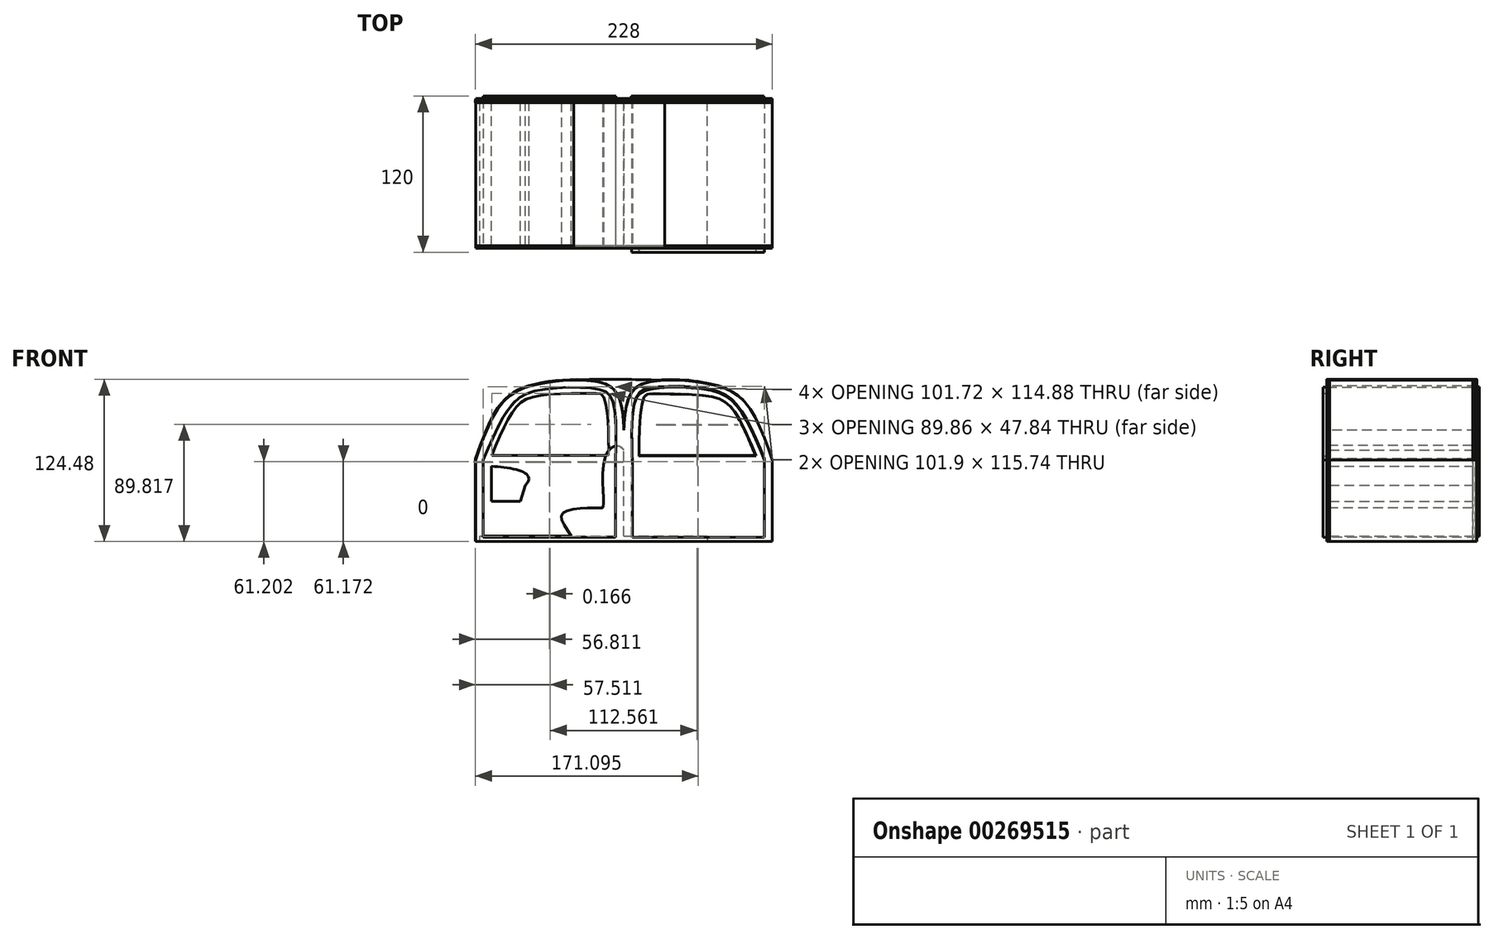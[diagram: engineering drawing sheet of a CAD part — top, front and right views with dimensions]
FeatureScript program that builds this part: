
annotation { "Feature Type Name" : "Feature", "Feature Type Description" : "" }
export const myFeature = defineFeature(function(context is Context, id is Id, definition is map)
    precondition{}
    {
        {
            var Q0;
            Q0=qCreatedBy(makeId("Front.planeOp"),FACE);
            var sketch = newSketch(context, id + "F0", { "sketchPlane" : qUnion([Q0])});
            skLineSegment(sketch, "E0.bottom", {"start": v(-52.37, -30.32) * mm, "end": v(58, -30.32) * mm});
            skLineSegment(sketch, "E0.top", {"start": v(-52.37, 75.93) * mm, "end": v(58, 75.93) * mm});
            skLineSegment(sketch, "E0.left", {"start": v(-52.37, -30.32) * mm, "end": v(-52.37, 75.93) * mm});
            skLineSegment(sketch, "E0.right", {"start": v(58, -30.32) * mm, "end": v(58, 75.93) * mm});
            skLineSegment(sketch, "E1", {"start": v(-52.37, -26.56) * mm, "end": v(17.83, -26.56) * mm});
            skFitSpline(sketch, "E2", {"points": [v(17.83, -26.56) * mm, v(11.64, -8.73) * mm, v(39.8, -5.16) * mm, v(42.43, -3.66) * mm, v(45.05, 37.08) * mm, v(58, 39.52) * mm, v(58, 9.86) * mm], "startDerivative": vector(-102.72, 146.21) * mm, "endDerivative": vector(-61.38, 44.33) * mm});
            skLineSegment(sketch, "E3", {"start": v(58, -26.56) * mm, "end": v(122.26, -26.56) * mm});
            skLineSegment(sketch, "E4", {"start": v(122.26, -26.56) * mm, "end": v(122.26, -30.32) * mm});
            skLineSegment(sketch, "E5", {"start": v(122.26, -30.32) * mm, "end": v(58, -30.32) * mm});
            skSolve(sketch);
        }
        {
            var Q0;
            {var subQ2=sQuery(id+"F0.wireOp",EDGE,"E0.bottom");Q0=makeQuery(id+"F0.imprint","IMPRINT",FACE,{"disambiguationData":[TD([[makeQuery(id+"F0.imprint","IMPRINT",EDGE,{"derivedFrom":subQ2}),1.0]])]});}
            var Q1;
            {var subQ2=sQuery(id+"F0.wireOp",EDGE,"E3");Q1=makeQuery(id+"F0.imprint","IMPRINT",FACE,{"disambiguationData":[TD([[makeQuery(id+"F0.imprint","IMPRINT",EDGE,{"derivedFrom":subQ2}),-1.0]])]});}
            var Q2;
            Q2=qSketchRegion(id+"F2",true);
            extrude(context, id + "F1", {"entities" : qUnion([Q0, Q1, Q2]), "endBound" : BoundingType.SYMMETRIC, "depth" : 110 * mm});
        }
        {
            var Q0;
            Q0=makeQuery(id+"F1.opExtrude","CAP_FACE",FACE,{"disambiguationData":[OSD([sQuery(id+"F0.wireOp",EDGE,"E0.bottom"),sQuery(id+"F0.wireOp",EDGE,"E0.left"),sQuery(id+"F0.wireOp",EDGE,"E0.right"),sQuery(id+"F0.wireOp",EDGE,"E1"),sQuery(id+"F0.wireOp",EDGE,"E2")])],"isStart":true});
            var sketch = newSketch(context, id + "F2", { "sketchPlane" : qUnion([Q0])});
            skLineSegment(sketch, "E6", {"start": v(21.37, 0) * mm, "end": v(17.65, 12.48) * mm});
            skFitSpline(sketch, "E7", {"points": [v(17.65, 12.48) * mm, v(14.83, 16.43) * mm, v(17.65, 21.68) * mm, v(43.55, 26.94) * mm, v(64.2, 27.5) * mm], "startDerivative": vector(-24.47, 23.82) * mm, "endDerivative": vector(59, 0.05) * mm});
            skPoint(sketch, "E8.right.end.orphan", {"position": v(30.41, 0) * mm});
            skLineSegment(sketch, "E9", {"start": v(21.37, 0) * mm, "end": v(43.55, 0) * mm});
            skLineSegment(sketch, "E10", {"start": v(43.55, 26.94) * mm, "end": v(43.55, 0) * mm});
            skSolve(sketch);
        }
        {
            var Q0;
            Q0=qSketchRegion(id+"F2",true);
            extrude(context, id + "F3", {"entities" : qUnion([Q0]), "oppositeDirection" : true, "depth" : 110 * mm});
        }
        {
            var Q0;
            Q0=makeQuery(id+"F1.opExtrude","CAP_FACE",FACE,{"disambiguationData":[OSD([sQuery(id+"F0.wireOp",EDGE,"E0.bottom"),sQuery(id+"F0.wireOp",EDGE,"E0.left"),sQuery(id+"F0.wireOp",EDGE,"E0.right"),sQuery(id+"F0.wireOp",EDGE,"E1"),sQuery(id+"F0.wireOp",EDGE,"E2"),sQuery(id+"F0.wireOp",EDGE,"E3"),sQuery(id+"F0.wireOp",EDGE,"E4"),sQuery(id+"F0.wireOp",EDGE,"E5")])],"isStart":false});
            var sketch = newSketch(context, id + "F4", { "sketchPlane" : qUnion([Q0])});
            skLineSegment(sketch, "E11.bottom", {"start": v(51.77, -27.48) * mm, "end": v(-49.8, -27.48) * mm});
            skLineSegment(sketch, "E11.left", {"start": v(51.77, -27.48) * mm, "end": v(51.77, 31.84) * mm});
            skLineSegment(sketch, "E11.right", {"start": v(-49.8, -27.48) * mm, "end": v(-49.8, 31.84) * mm});
            skFitSpline(sketch, "E12", {"points": [v(-49.8, 31.84) * mm, v(-29.14, 72.58) * mm, v(-8.12, 85.15) * mm, v(37.12, 86.28) * mm, v(48.95, 78.58) * mm, v(51.77, 31.84) * mm], "startDerivative": vector(85.44, 201.79) * mm, "endDerivative": vector(-6.45, -241.46) * mm});
            skLineSegment(sketch, "E13.top", {"start": v(-55.74, -30.78) * mm, "end": v(58.17, -30.78) * mm});
            skLineSegment(sketch, "E13.left", {"start": v(-55.74, 31.84) * mm, "end": v(-55.74, -30.78) * mm});
            skLineSegment(sketch, "E13.right", {"start": v(58.17, 31.84) * mm, "end": v(58.17, -30.78) * mm});
            skFitSpline(sketch, "E14", {"points": [v(-55.74, 31.84) * mm, v(-35.95, 74.78) * mm, v(-9.12, 89.73) * mm, v(37.12, 91.93) * mm, v(53.77, 80.94) * mm, v(58.17, 31.84) * mm], "startDerivative": vector(76.78, 219.74) * mm, "endDerivative": vector(-3.68, -254.2) * mm});
            skFitSpline(sketch, "E15.MirrorCS", {"points": [v(172.09, 31.84) * mm, v(152.3, 74.78) * mm, v(125.47, 89.73) * mm, v(79.22, 91.93) * mm, v(62.57, 80.94) * mm, v(58.17, 31.84) * mm], "startDerivative": vector(-76.78, 219.74) * mm, "endDerivative": vector(3.68, -254.2) * mm});
            skFitSpline(sketch, "E16.MirrorCS", {"points": [v(166.14, 31.84) * mm, v(145.49, 72.58) * mm, v(124.46, 85.15) * mm, v(79.22, 86.28) * mm, v(67.4, 78.58) * mm, v(64.58, 31.84) * mm], "startDerivative": vector(-85.44, 201.79) * mm, "endDerivative": vector(6.45, -241.46) * mm});
            skLineSegment(sketch, "E17.MirrorCS", {"start": v(64.58, -27.48) * mm, "end": v(64.58, 31.84) * mm});
            skLineSegment(sketch, "E18.MirrorCS", {"start": v(64.58, -27.48) * mm, "end": v(166.14, -27.48) * mm});
            skLineSegment(sketch, "E19.MirrorCS", {"start": v(172.09, -30.78) * mm, "end": v(58.17, -30.78) * mm});
            skLineSegment(sketch, "E20.MirrorCS", {"start": v(172.09, 31.84) * mm, "end": v(172.09, -30.78) * mm});
            skLineSegment(sketch, "E21.MirrorCS", {"start": v(166.14, -27.48) * mm, "end": v(166.14, 31.84) * mm});
            skLineSegment(sketch, "E22.right", {"start": v(58.42, 31.84) * mm, "end": v(58.42, -30.78) * mm});
            skFitSpline(sketch, "E23", {"points": [v(-49.8, 31.84) * mm, v(-29.14, 72.58) * mm, v(-8.12, 85.15) * mm, v(37.12, 86.28) * mm, v(48.95, 78.58) * mm, v(51.77, 31.84) * mm], "startDerivative": vector(85.44, 201.79) * mm, "endDerivative": vector(-6.45, -241.46) * mm});
            skFitSpline(sketch, "E24", {"points": [v(-43.16, 34.84) * mm, v(-25.58, 70.51) * mm, v(-8.12, 80.46) * mm, v(34.68, 82.53) * mm, v(43.5, 78.2) * mm, v(46.7, 34.66) * mm, v(46.7, 34.47) * mm], "startDerivative": vector(74.67, 181.05) * mm, "endDerivative": vector(0.05, -3.93) * mm});
            skLineSegment(sketch, "E25", {"start": v(-43.16, 34.84) * mm, "end": v(46.7, 34.66) * mm});
            skLineSegment(sketch, "E26.left", {"start": v(64.58, -26.56) * mm, "end": v(64.58, 32.76) * mm});
            skFitSpline(sketch, "E27.MirrorCS", {"points": [v(159.5, 35.76) * mm, v(141.92, 71.43) * mm, v(124.46, 81.38) * mm, v(81.66, 83.44) * mm, v(72.84, 79.13) * mm, v(69.65, 35.57) * mm, v(69.65, 35.39) * mm], "startDerivative": vector(-74.67, 181.05) * mm, "endDerivative": vector(-0.05, -3.93) * mm});
            skLineSegment(sketch, "E28.MirrorCS", {"start": v(159.5, 35.76) * mm, "end": v(69.65, 35.57) * mm});
            skFitSpline(sketch, "E29.MirrorCS", {"points": [v(166.14, 32.76) * mm, v(145.49, 73.5) * mm, v(124.46, 86.07) * mm, v(79.22, 87.2) * mm, v(67.4, 79.5) * mm, v(64.58, 32.76) * mm], "startDerivative": vector(-85.44, 201.79) * mm, "endDerivative": vector(6.45, -241.46) * mm});
            skLineSegment(sketch, "E30.MirrorCS", {"start": v(166.14, -26.56) * mm, "end": v(166.14, 32.76) * mm});
            skLineSegment(sketch, "E31.MirrorCS", {"start": v(64.58, -26.56) * mm, "end": v(166.14, -26.56) * mm});
            skSolve(sketch);
        }
        {
            var Q0;
            Q0=qSketchRegion(id+"F4",true);
            extrude(context, id + "F5", {"entities" : qUnion([Q0]), "depth" : 2 * mm});
        }
        {
            var Q0;
            Q0=makeQuery(id+"F1.opExtrude","CAP_FACE",FACE,{"disambiguationData":[OSD([sQuery(id+"F0.wireOp",EDGE,"E0.bottom"),sQuery(id+"F0.wireOp",EDGE,"E0.left"),sQuery(id+"F0.wireOp",EDGE,"E0.right"),sQuery(id+"F0.wireOp",EDGE,"E1"),sQuery(id+"F0.wireOp",EDGE,"E2"),sQuery(id+"F0.wireOp",EDGE,"E3"),sQuery(id+"F0.wireOp",EDGE,"E4"),sQuery(id+"F0.wireOp",EDGE,"E5")])],"isStart":true});
            var sketch = newSketch(context, id + "F6", { "sketchPlane" : qUnion([Q0])});
            skLineSegment(sketch, "E32.right", {"start": v(-58, 32.3) * mm, "end": v(-58, -30.32) * mm});
            skFitSpline(sketch, "E33.MirrorCS", {"points": [v(55.9, 32.3) * mm, v(36.12, 75.24) * mm, v(9.29, 90.2) * mm, v(-36.96, 92.4) * mm, v(-53.6, 81.4) * mm, v(-58, 32.3) * mm], "startDerivative": vector(-76.78, 219.74) * mm, "endDerivative": vector(3.68, -254.2) * mm});
            skFitSpline(sketch, "E34.MirrorCS", {"points": [v(49.96, 32.3) * mm, v(29.3, 73.04) * mm, v(8.28, 85.62) * mm, v(-36.96, 86.74) * mm, v(-48.78, 79.05) * mm, v(-51.6, 32.3) * mm], "startDerivative": vector(-85.44, 201.79) * mm, "endDerivative": vector(6.45, -241.46) * mm});
            skLineSegment(sketch, "E35.MirrorCS", {"start": v(-51.6, -27.02) * mm, "end": v(-51.6, 32.3) * mm});
            skLineSegment(sketch, "E36.MirrorCS", {"start": v(-51.6, -27.02) * mm, "end": v(49.96, -27.02) * mm});
            skLineSegment(sketch, "E37.MirrorCS", {"start": v(55.9, -30.32) * mm, "end": v(-58, -30.32) * mm});
            skLineSegment(sketch, "E38.MirrorCS", {"start": v(55.9, 32.3) * mm, "end": v(55.9, -30.32) * mm});
            skLineSegment(sketch, "E39.MirrorCS", {"start": v(49.96, -27.02) * mm, "end": v(49.96, 32.3) * mm});
            skLineSegment(sketch, "E40.MirrorCS", {"start": v(-58.32, 32.3) * mm, "end": v(-58.32, -30.32) * mm});
            skLineSegment(sketch, "E41.bottom", {"start": v(-64.16, -27.02) * mm, "end": v(-165.72, -27.02) * mm});
            skLineSegment(sketch, "E41.left", {"start": v(-64.16, -27.02) * mm, "end": v(-64.16, 32.3) * mm});
            skLineSegment(sketch, "E41.right", {"start": v(-165.72, -27.02) * mm, "end": v(-165.72, 32.3) * mm});
            skFitSpline(sketch, "E42", {"points": [v(-165.72, 32.3) * mm, v(-145.07, 73.04) * mm, v(-124.05, 85.62) * mm, v(-78.8, 86.74) * mm, v(-66.98, 79.05) * mm, v(-64.16, 32.3) * mm], "startDerivative": vector(85.44, 201.79) * mm, "endDerivative": vector(-6.45, -241.46) * mm});
            skLineSegment(sketch, "E43.left", {"start": v(-171.67, 32.3) * mm, "end": v(-171.67, -30.32) * mm});
            skLineSegment(sketch, "E43.right", {"start": v(-57.76, 32.3) * mm, "end": v(-57.76, -30.32) * mm});
            skFitSpline(sketch, "E44", {"points": [v(-171.67, 32.3) * mm, v(-151.88, 75.24) * mm, v(-125.05, 90.2) * mm, v(-78.8, 92.4) * mm, v(-62.16, 81.4) * mm, v(-57.76, 32.3) * mm], "startDerivative": vector(76.78, 219.74) * mm, "endDerivative": vector(-3.68, -254.2) * mm});
            skLineSegment(sketch, "E45.MirrorCS", {"start": v(-171.67, -30.32) * mm, "end": v(-57.76, -30.32) * mm});
            skSolve(sketch);
        }
        {
            var Q0;
            Q0=qSketchRegion(id+"F6",true);
            extrude(context, id + "F7", {"entities" : qUnion([Q0]), "depth" : 2 * mm});
        }
        {
            var Q0;
            Q0=makeQuery(id+"F7.opExtrude","CAP_FACE",FACE,{"disambiguationData":[OSD([sQuery(id+"F6.wireOp",EDGE,"E33.MirrorCS"),sQuery(id+"F6.wireOp",EDGE,"E34.MirrorCS"),sQuery(id+"F6.wireOp",EDGE,"E35.MirrorCS"),sQuery(id+"F6.wireOp",EDGE,"E36.MirrorCS"),sQuery(id+"F6.wireOp",EDGE,"E37.MirrorCS"),sQuery(id+"F6.wireOp",EDGE,"E38.MirrorCS"),sQuery(id+"F6.wireOp",EDGE,"E39.MirrorCS"),sQuery(id+"F6.wireOp",EDGE,"E41.bottom"),sQuery(id+"F6.wireOp",EDGE,"E41.left"),sQuery(id+"F6.wireOp",EDGE,"E41.right"),sQuery(id+"F6.wireOp",EDGE,"E42"),sQuery(id+"F6.wireOp",EDGE,"E43.left"),sQuery(id+"F6.wireOp",EDGE,"E44"),sQuery(id+"F6.wireOp",EDGE,"E45.MirrorCS")])],"isStart":false});
            var sketch = newSketch(context, id + "F8", { "sketchPlane" : qUnion([Q0])});
            skLineSegment(sketch, "E46.bottom", {"start": v(-64.16, -27.02) * mm, "end": v(-165.72, -27.02) * mm});
            skLineSegment(sketch, "E46.right", {"start": v(-165.72, -27.02) * mm, "end": v(-165.72, 32.3) * mm});
            skFitSpline(sketch, "E47", {"points": [v(-165.72, 32.3) * mm, v(-145.07, 73.04) * mm, v(-124.05, 85.62) * mm, v(-78.8, 86.74) * mm, v(-66.98, 79.05) * mm, v(-64.16, 32.3) * mm], "startDerivative": vector(85.44, 201.79) * mm, "endDerivative": vector(-6.45, -241.46) * mm});
            skFitSpline(sketch, "E48", {"points": [v(-159.1, 35.3) * mm, v(-141.5, 70.97) * mm, v(-124.05, 80.92) * mm, v(-81.25, 82.99) * mm, v(-72.42, 78.67) * mm, v(-69.23, 35.12) * mm, v(-69.23, 34.93) * mm], "startDerivative": vector(74.67, 181.05) * mm, "endDerivative": vector(0.05, -3.93) * mm});
            skLineSegment(sketch, "E49", {"start": v(-159.1, 35.3) * mm, "end": v(-69.23, 35.12) * mm});
            skLineSegment(sketch, "E50.left", {"start": v(-51.6, -27.02) * mm, "end": v(-51.6, 32.3) * mm});
            skFitSpline(sketch, "E51.MirrorCS", {"points": [v(43.33, 35.3) * mm, v(25.74, 70.97) * mm, v(8.28, 80.92) * mm, v(-34.52, 82.99) * mm, v(-43.34, 78.67) * mm, v(-46.53, 35.12) * mm, v(-46.53, 34.93) * mm], "startDerivative": vector(-74.67, 181.05) * mm, "endDerivative": vector(-0.05, -3.93) * mm});
            skLineSegment(sketch, "E52.MirrorCS", {"start": v(43.33, 35.3) * mm, "end": v(-46.53, 35.12) * mm});
            skFitSpline(sketch, "E53.MirrorCS", {"points": [v(49.96, 32.3) * mm, v(29.3, 73.04) * mm, v(8.28, 85.62) * mm, v(-36.96, 86.74) * mm, v(-48.78, 79.05) * mm, v(-51.6, 32.3) * mm], "startDerivative": vector(-85.44, 201.79) * mm, "endDerivative": vector(6.45, -241.46) * mm});
            skLineSegment(sketch, "E54.MirrorCS", {"start": v(49.96, -27.02) * mm, "end": v(49.96, 32.3) * mm});
            skLineSegment(sketch, "E55.MirrorCS", {"start": v(-51.6, -27.02) * mm, "end": v(49.96, -27.02) * mm});
            skLineSegment(sketch, "E56", {"start": v(-64.16, 32.3) * mm, "end": v(-64.16, -27.02) * mm});
            skSolve(sketch);
        }
        {
            var Q0;
            Q0=makeQuery(id+"F8.imprint","IMPRINT",FACE,{"disambiguationData":[TD([[makeQuery(id+"F8.imprint","IMPRINT",EDGE,{"derivedFrom":sQuery(id+"F8.wireOp",EDGE,"E46.bottom")}),-1.0]])]});
            var Q1;
            Q1=makeQuery(id+"F8.imprint","IMPRINT",FACE,{"disambiguationData":[TD([[makeQuery(id+"F8.imprint","IMPRINT",EDGE,{"derivedFrom":sQuery(id+"F8.wireOp",EDGE,"E50.left")}),-1.0]])]});
            extrude(context, id + "F9", {"entities" : qUnion([Q0, Q1]), "depth" : 3 * mm});
        }
        {
            var Q0;
            Q0=makeQuery(id+"F5.opExtrude","CAP_FACE",FACE,{"disambiguationData":[OSD([sQuery(id+"F4.wireOp",EDGE,"E13.left"),sQuery(id+"F4.wireOp",EDGE,"E14"),sQuery(id+"F4.wireOp",EDGE,"E13.top"),sQuery(id+"F4.wireOp",EDGE,"E15.MirrorCS"),sQuery(id+"F4.wireOp",EDGE,"E16.MirrorCS"),sQuery(id+"F4.wireOp",EDGE,"E17.MirrorCS"),sQuery(id+"F4.wireOp",EDGE,"E18.MirrorCS"),sQuery(id+"F4.wireOp",EDGE,"E19.MirrorCS"),sQuery(id+"F4.wireOp",EDGE,"E20.MirrorCS"),sQuery(id+"F4.wireOp",EDGE,"E21.MirrorCS"),sQuery(id+"F4.wireOp",EDGE,"E11.bottom"),sQuery(id+"F4.wireOp",EDGE,"E11.left"),sQuery(id+"F4.wireOp",EDGE,"E11.right"),sQuery(id+"F4.wireOp",EDGE,"E23"),sQuery(id+"F4.wireOp",EDGE,"E26.left"),sQuery(id+"F4.wireOp",EDGE,"E29.MirrorCS"),sQuery(id+"F4.wireOp",EDGE,"E30.MirrorCS")])],"isStart":false});
            var sketch = newSketch(context, id + "F10", { "sketchPlane" : qUnion([Q0])});
            skLineSegment(sketch, "E57.left", {"start": v(64.58, -27.48) * mm, "end": v(64.58, 31.84) * mm});
            skFitSpline(sketch, "E58.MirrorCS", {"points": [v(159.5, 34.84) * mm, v(141.92, 70.51) * mm, v(124.46, 80.46) * mm, v(81.66, 82.53) * mm, v(72.84, 78.2) * mm, v(69.65, 34.66) * mm, v(69.65, 34.47) * mm], "startDerivative": vector(-74.67, 181.05) * mm, "endDerivative": vector(-0.05, -3.93) * mm});
            skLineSegment(sketch, "E59.MirrorCS", {"start": v(159.5, 34.84) * mm, "end": v(69.65, 34.66) * mm});
            skFitSpline(sketch, "E60.MirrorCS", {"points": [v(166.14, 31.84) * mm, v(145.49, 72.58) * mm, v(124.46, 85.15) * mm, v(79.22, 86.28) * mm, v(67.4, 78.58) * mm, v(64.58, 31.84) * mm], "startDerivative": vector(-85.44, 201.79) * mm, "endDerivative": vector(6.45, -241.46) * mm});
            skLineSegment(sketch, "E61.MirrorCS", {"start": v(166.14, -27.48) * mm, "end": v(166.14, 31.84) * mm});
            skLineSegment(sketch, "E62.MirrorCS", {"start": v(64.58, -27.48) * mm, "end": v(166.14, -27.48) * mm});
            skFitSpline(sketch, "E63", {"points": [v(-17.9, 87.2) * mm, v(19.69, 93.08) * mm, v(89.33, 92.98) * mm, v(108.24, 92.43) * mm], "startDerivative": vector(98.6, 27.18) * mm, "endDerivative": vector(54.95, -2.18) * mm});
            skSolve(sketch);
        }
        {
            var Q0;
            {var subQ5=sQuery(id+"F10.wireOp",EDGE,"E57.left");Q0=makeQuery(id+"F10.imprint","IMPRINT",FACE,{"disambiguationData":[TD([[makeQuery(id+"F10.imprint","IMPRINT",EDGE,{"derivedFrom":subQ5}),-1.0]])]});}
            extrude(context, id + "F11", {"entities" : qUnion([Q0]), "depth" : 3 * mm});
        }
        {
            var Q0;
            {var subQ0=sQuery(id+"F10.wireOp",EDGE,"E63");var subQ1=makeQuery(id+"F5.opExtrude","CAP_EDGE",EDGE,{"disambiguationData":[OSD([sQuery(id+"F4.wireOp",EDGE,"E14")])],"isStart":false});var subQ2=makeQuery(id+"F10.imprint","INTERSECT",VERTEX,{"disambiguationData":[OD(1.0)],"derivedFrom":[subQ1,subQ0]});Q0=makeQuery(id+"F10.imprint","IMPRINT",FACE,{"disambiguationData":[TD([[makeQuery(id+"F10.imprint","IMPRINT",EDGE,{"disambiguationData":[TD([[subQ2,-1.0]])],"derivedFrom":subQ0}),-1.0]])]});}
            var Q1;
            Q1=makeQuery(id+"F5.opExtrude","CAP_FACE",FACE,{"disambiguationData":[OSD([sQuery(id+"F4.wireOp",EDGE,"E13.left"),sQuery(id+"F4.wireOp",EDGE,"E14"),sQuery(id+"F4.wireOp",EDGE,"E13.top"),sQuery(id+"F4.wireOp",EDGE,"E15.MirrorCS"),sQuery(id+"F4.wireOp",EDGE,"E16.MirrorCS"),sQuery(id+"F4.wireOp",EDGE,"E17.MirrorCS"),sQuery(id+"F4.wireOp",EDGE,"E18.MirrorCS"),sQuery(id+"F4.wireOp",EDGE,"E19.MirrorCS"),sQuery(id+"F4.wireOp",EDGE,"E20.MirrorCS"),sQuery(id+"F4.wireOp",EDGE,"E21.MirrorCS"),sQuery(id+"F4.wireOp",EDGE,"E11.bottom"),sQuery(id+"F4.wireOp",EDGE,"E11.left"),sQuery(id+"F4.wireOp",EDGE,"E11.right"),sQuery(id+"F4.wireOp",EDGE,"E23"),sQuery(id+"F4.wireOp",EDGE,"E26.left"),sQuery(id+"F4.wireOp",EDGE,"E29.MirrorCS"),sQuery(id+"F4.wireOp",EDGE,"E30.MirrorCS")])],"isStart":false});
            var Q2;
            Q2=sQuery(id+"F10.wireOp",EDGE,"E63");
            extrude(context, id + "F12", {"entities" : qUnion([Q0, Q1]), "surfaceEntities" : qUnion([Q2]), "oppositeDirection" : true, "depth" : 115 * mm});
        }
    });
